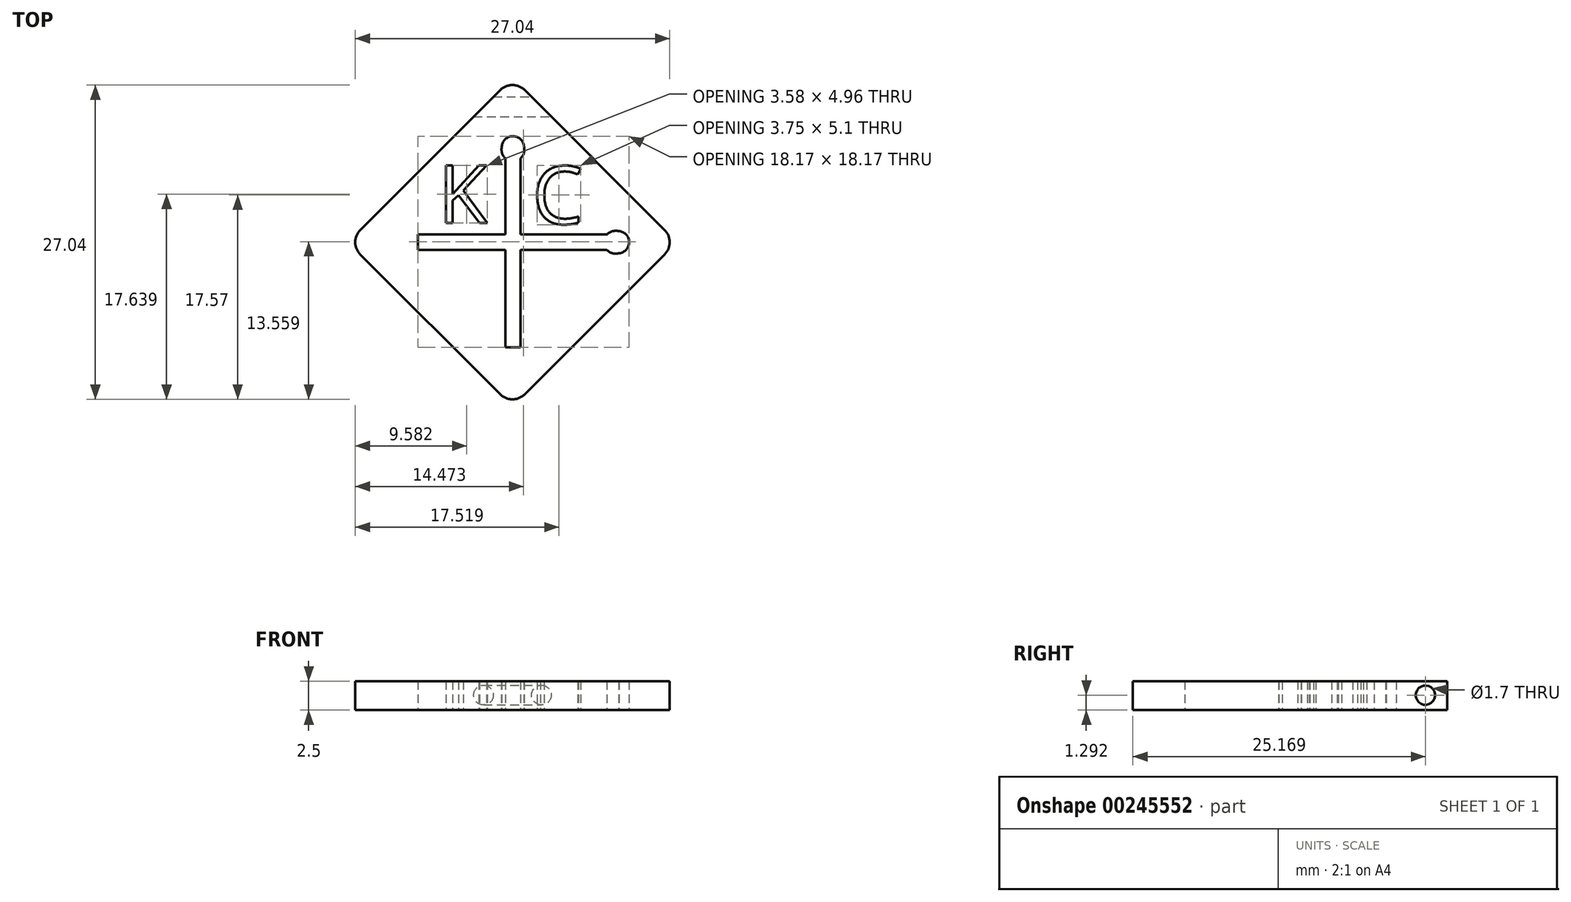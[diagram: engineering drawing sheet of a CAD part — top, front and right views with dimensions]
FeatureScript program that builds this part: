
annotation { "Feature Type Name" : "Feature", "Feature Type Description" : "" }
export const myFeature = defineFeature(function(context is Context, id is Id, definition is map)
    precondition{}
    {
        {
            var Q0;
            Q0=qCreatedBy(makeId("Top.planeOp"),FACE);
            var sketch = newSketch(context, id + "F0", { "sketchPlane" : qUnion([Q0])});
            skLineSegment(sketch, "E0", {"start": v(1.06, -1.06) * mm, "end": v(13.08, -13.08) * mm});
            skLineSegment(sketch, "E1", {"start": v(13.08, -15.2) * mm, "end": v(1.06, -27.22) * mm});
            skLineSegment(sketch, "E2", {"start": v(-1.06, -27.22) * mm, "end": v(-13.08, -15.2) * mm});
            skLineSegment(sketch, "E3", {"start": v(-13.08, -13.08) * mm, "end": v(-1.06, -1.06) * mm});
            skPoint(sketch, "E4.visualSharp", {"position": v(0, 0) * mm});
            skArc(sketch, "E4.filletArc", {"start": v(1.06, -1.06) * mm, "mid": v(0, -0.62) * mm, "end": v(-1.06, -1.06) * mm});
            skPoint(sketch, "E5.visualSharp", {"position": v(-14.14, -14.14) * mm});
            skArc(sketch, "E5.filletArc", {"start": v(-13.08, -13.08) * mm, "mid": v(-13.52, -14.14) * mm, "end": v(-13.08, -15.2) * mm});
            skPoint(sketch, "E6.visualSharp", {"position": v(14.14, -14.14) * mm});
            skArc(sketch, "E6.filletArc", {"start": v(13.08, -15.2) * mm, "mid": v(13.52, -14.14) * mm, "end": v(13.08, -13.08) * mm});
            skPoint(sketch, "E7.visualSharp", {"position": v(0, -28.28) * mm});
            skArc(sketch, "E7.filletArc", {"start": v(-1.06, -27.22) * mm, "mid": v(0, -27.66) * mm, "end": v(1.06, -27.22) * mm});
            skLineSegment(sketch, "E8", {"start": v(0, 0) * mm, "end": v(0, -31.86) * mm, "construction": true});
            skLineSegment(sketch, "E9", {"start": v(-14.14, -14.14) * mm, "end": v(14.14, -14.14) * mm, "construction": true});
            skLineSegment(sketch, "E10", {"start": v(-8.13, -13.48) * mm, "end": v(-8.13, -14.8) * mm});
            skLineSegment(sketch, "E11", {"start": v(-8.13, -14.8) * mm, "end": v(8.13, -14.8) * mm});
            skLineSegment(sketch, "E12", {"start": v(8.13, -13.48) * mm, "end": v(-8.13, -13.48) * mm});
            skLineSegment(sketch, "E13", {"start": v(-8.13, -13.48) * mm, "end": v(0, -13.48) * mm, "construction": true});
            skLineSegment(sketch, "E14", {"start": v(0, -13.48) * mm, "end": v(8.13, -13.48) * mm, "construction": true});
            skArc(sketch, "E15", {"start": v(9.18, -15.1) * mm, "mid": v(10.04, -14.12) * mm, "end": v(9.13, -13.2) * mm});
            skArc(sketch, "E16", {"start": v(9.13, -13.2) * mm, "mid": v(8.6, -13.2) * mm, "end": v(8.13, -13.48) * mm});
            skArc(sketch, "E17", {"start": v(8.13, -14.8) * mm, "mid": v(8.61, -15.1) * mm, "end": v(9.18, -15.1) * mm});
            skLineSegment(sketch, "E18", {"start": v(-0.62, -23.19) * mm, "end": v(0.7, -23.19) * mm});
            skLineSegment(sketch, "E19", {"start": v(0.7, -23.19) * mm, "end": v(0.7, -6.92) * mm});
            skLineSegment(sketch, "E20", {"start": v(-0.62, -6.92) * mm, "end": v(-0.62, -23.19) * mm});
            skLineSegment(sketch, "E21", {"start": v(-0.62, -23.19) * mm, "end": v(-0.62, -15.05) * mm, "construction": true});
            skLineSegment(sketch, "E22", {"start": v(-0.62, -15.05) * mm, "end": v(-0.62, -6.92) * mm, "construction": true});
            skArc(sketch, "E23", {"start": v(0.99, -5.88) * mm, "mid": v(0.02, -5.01) * mm, "end": v(-0.91, -5.92) * mm});
            skArc(sketch, "E24", {"start": v(-0.91, -5.92) * mm, "mid": v(-0.9, -6.46) * mm, "end": v(-0.62, -6.92) * mm});
            skArc(sketch, "E25", {"start": v(0.7, -6.92) * mm, "mid": v(1, -6.44) * mm, "end": v(0.99, -5.88) * mm});
            skText(sketch, "E26", { "text": "K", "fontName": "OpenSans-Regular.ttf"});
            skText(sketch, "E27", { "text": "C", "fontName": "OpenSans-Regular.ttf"});
            const initialGuessF0  = {"E26": [-0.00641, -0.0125, 1, 0, 0.005], "E27": [0.0017, -0.01257, 1, 0, 0.005]};
            skSetInitialGuess(sketch, initialGuessF0);
            skSolve(sketch);
        }
        {
            var Q0;
            Q0=makeQuery(id+"F0.imprint","IMPRINT",FACE,{"disambiguationData":[TD([[makeQuery(id+"F0.imprint","IMPRINT",EDGE,{"derivedFrom":sQuery(id+"F0.wireOp",EDGE,"E0")}),-1.0]])]});
            extrude(context, id + "F1", {"entities" : qUnion([Q0]), "depth" : 2.5 * mm});
        }
        {
            var Q0;
            Q0=qCreatedBy(makeId("Right.planeOp"),FACE);
            var sketch = newSketch(context, id + "F2", { "sketchPlane" : qUnion([Q0])});
            skCircle(sketch, "E28", {"center": v(-2.5, 1.3) * mm, "radius": 0.85 * mm});
            skSolve(sketch);
        }
        {
            var Q0;
            Q0=qSketchRegion(id+"F2",true);
            extrude(context, id + "F3", {"entities" : qUnion([Q0]), "operationType" : NewBodyOperationType.REMOVE, "endBound" : BoundingType.SYMMETRIC, "oppositeDirection" : true, "depth" : 25 * mm});
        }
    });
